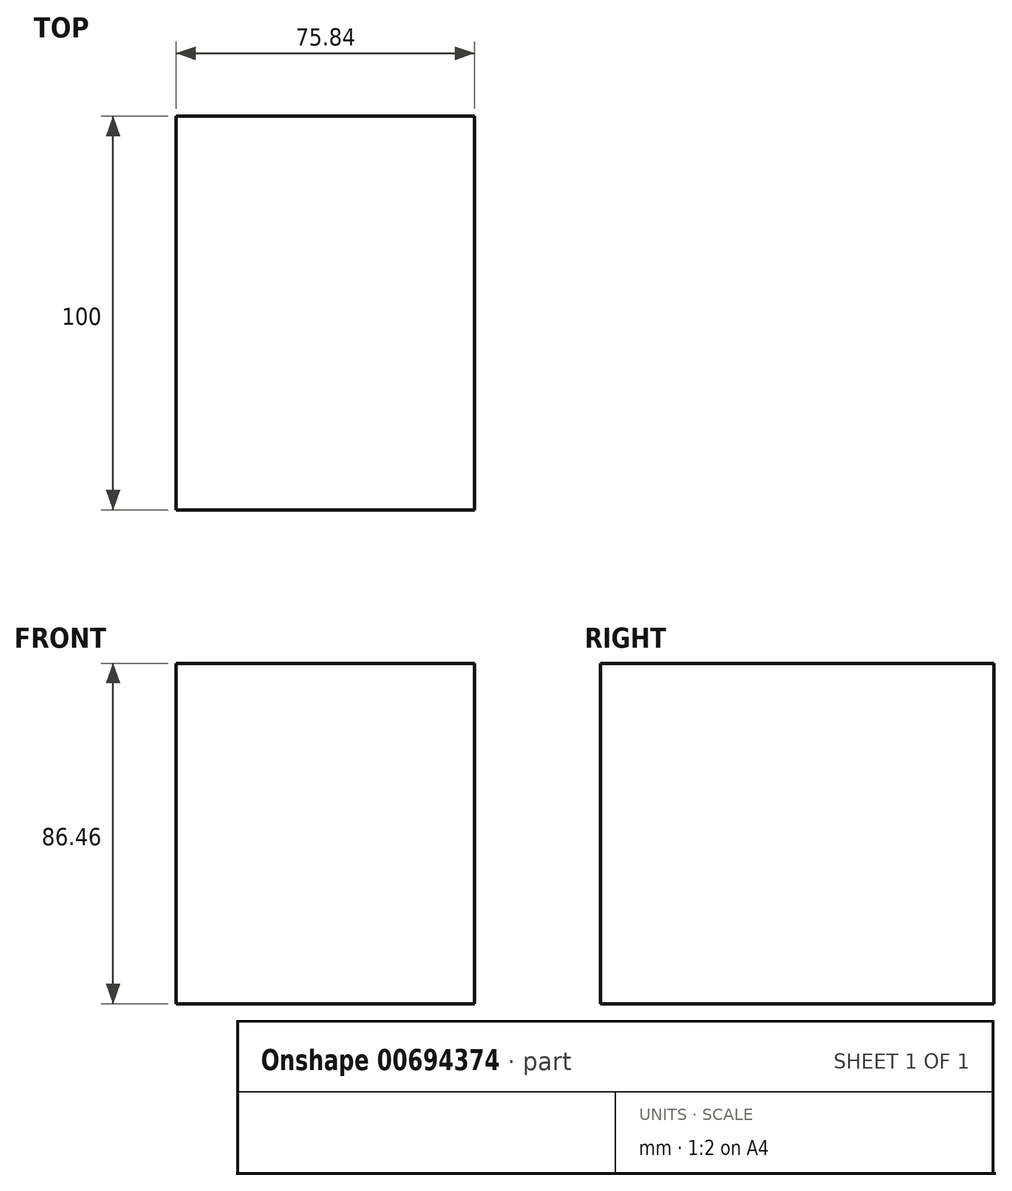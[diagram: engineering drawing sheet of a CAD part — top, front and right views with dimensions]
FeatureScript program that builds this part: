
annotation { "Feature Type Name" : "Feature", "Feature Type Description" : "" }
export const myFeature = defineFeature(function(context is Context, id is Id, definition is map)
    precondition{}
    {
        {
            var Q0;
            Q0=qCreatedBy(makeId("Front.planeOp"),FACE);
            var sketch = newSketch(context, id + "F0", { "sketchPlane" : qUnion([Q0])});
            skLineSegment(sketch, "E0.bottom", {"start": v(-37.92, 43.23) * mm, "end": v(37.92, 43.23) * mm});
            skLineSegment(sketch, "E0.top", {"start": v(-37.92, -43.23) * mm, "end": v(37.92, -43.23) * mm});
            skLineSegment(sketch, "E0.left", {"start": v(-37.92, 43.23) * mm, "end": v(-37.92, -43.23) * mm});
            skLineSegment(sketch, "E0.right", {"start": v(37.92, 43.23) * mm, "end": v(37.92, -43.23) * mm});
            skPoint(sketch, "E0.middle", {"position": v(0, 0) * mm});
            skSolve(sketch);
        }
        {
            var Q0;
            Q0 = qSketchRegion(id + "F0", true);
            extrude(context, id + "F1", {"entities" : qUnion([Q0]), "depth" : 100 * mm, "offsetDistance" : 25.4 * mm});
        }
    });
